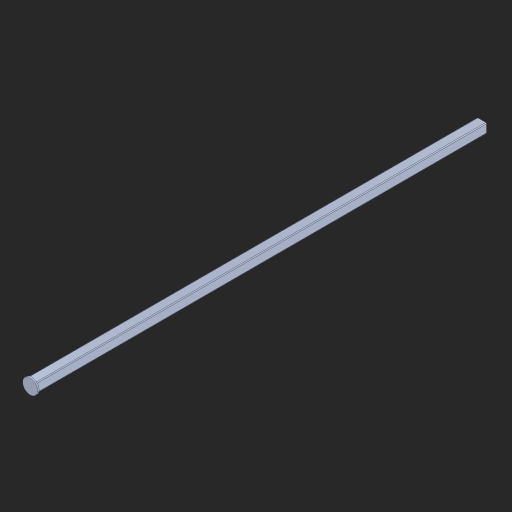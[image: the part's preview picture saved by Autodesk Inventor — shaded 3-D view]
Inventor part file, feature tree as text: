
AUTODESK INVENTOR PART (.ipt)
format: ipt  version: 2023 (Build 270158000, 158)  size: 174,592 bytes
history: native  units: in
note: dims shown in document units (in); Inventor stores cm internally (conversion verified against a paired STEP export)
features: other x14, extrude x2, sketch x2
ambient origin geometry x8: Origin, YZ Plane, XZ Plane, XY Plane, X Axis, Y Axis, Z Axis, Center Point
bodies: Solid1 (feature_tree)
feature tree (18):
  other  "Table"
  other  "Shaft LS Capped 6.0"
  other  "Shaft LS Capped 5.5"
  other  "Shaft LS Capped 5.0"
  other  "Shaft LS Capped 4.5"
  other  "Shaft LS Capped 4.0"
  other  "Shaft LS Capped 3.5"
  other  "Shaft LS Capped 3.0"
  other  "Shaft LS Capped 2.5"
  other  "Shaft LS Capped 2.0"
  other  "Shaft LS Capped 1.5"
  other  "Shaft LS Capped 1.0"
  other  "Shaft LS Capped 0.5"
  extrude  "Extrusion3"  Depth=6.0in
  extrude  "Extrusion4"  [1 undecoded]
  sketch  "Sketch4"  dims[d10=6.0in d11=0.0in d12=0.2in]
  sketch  "Sketch5"  dims[d13=0.02in d14=0.0in]
  parser-record x1  (decoder bookkeeping rows leaked as tree rows — omitted from the tree; the rows remain in map.json)
note: 1 required parameter value undecoded (feature->parameter linkage not recoverable at this tier; creation-order binding heuristic only, values carry confidence <= 0.55)
